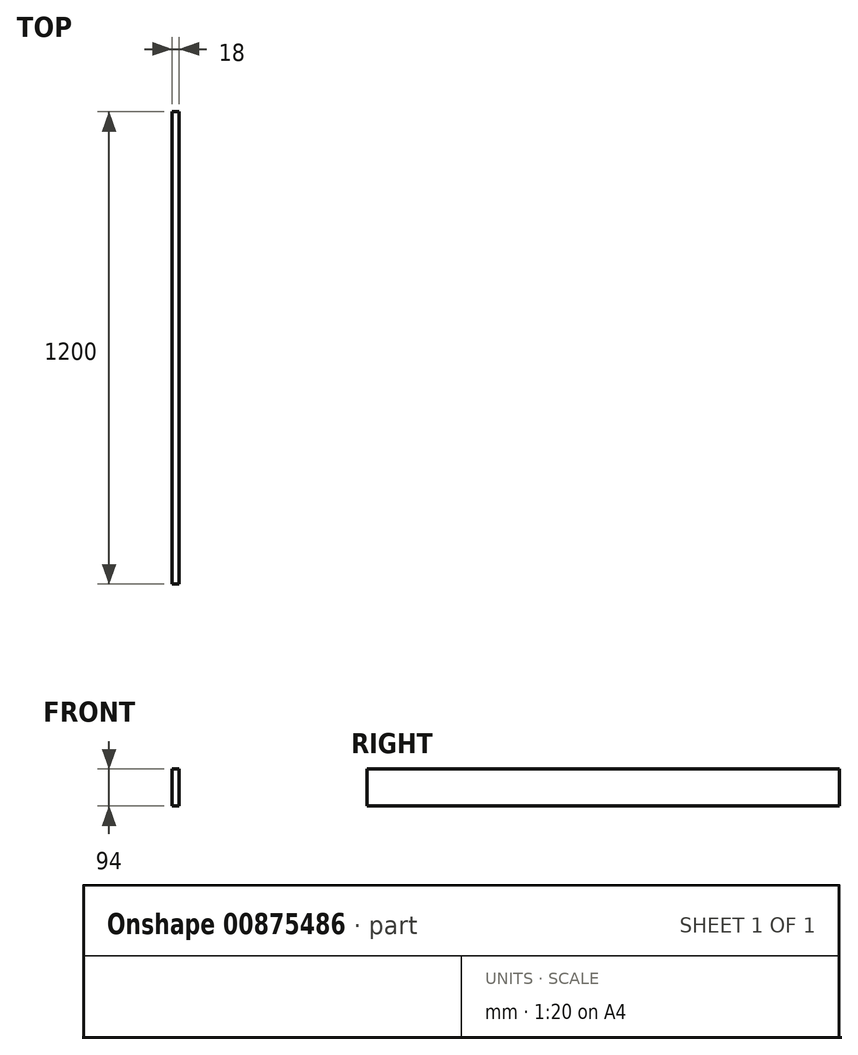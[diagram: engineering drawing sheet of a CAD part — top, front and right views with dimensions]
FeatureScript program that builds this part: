
annotation { "Feature Type Name" : "Feature", "Feature Type Description" : "" }
export const myFeature = defineFeature(function(context is Context, id is Id, definition is map)
    precondition{}
    {
        {
            var Q0;
            Q0=qCreatedBy(makeId("Front.planeOp"),FACE);
            var sketch = newSketch(context, id + "F0", { "sketchPlane" : qUnion([Q0])});
            skLineSegment(sketch, "E0.bottom", {"start": v(0, 0) * mm, "end": v(18, 0) * mm});
            skLineSegment(sketch, "E0.top", {"start": v(0, 94) * mm, "end": v(18, 94) * mm});
            skLineSegment(sketch, "E0.left", {"start": v(0, 0) * mm, "end": v(0, 94) * mm});
            skLineSegment(sketch, "E0.right", {"start": v(18, 0) * mm, "end": v(18, 94) * mm});
            skSolve(sketch);
        }
        {
            var Q0;
            Q0 = qSketchRegion(id + "F0", true);
            extrude(context, id + "F1", {"entities" : qUnion([Q0]), "depth" : 1200 * mm, "offsetDistance" : 25 * mm});
        }
    });
